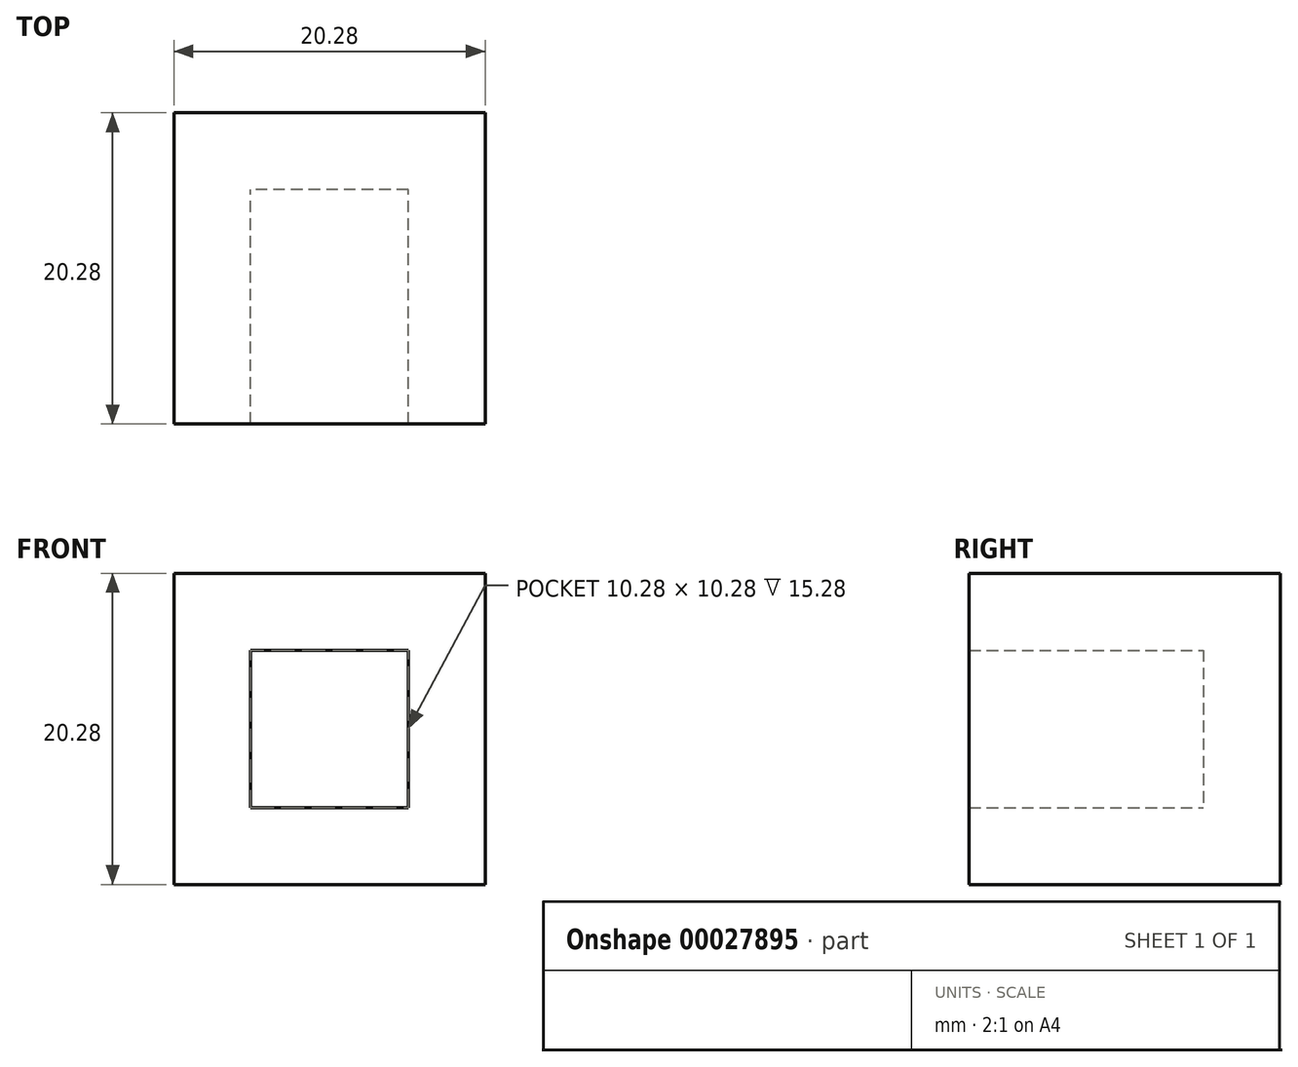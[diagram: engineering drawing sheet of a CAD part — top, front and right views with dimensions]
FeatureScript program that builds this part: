
annotation { "Feature Type Name" : "Feature", "Feature Type Description" : "" }
export const myFeature = defineFeature(function(context is Context, id is Id, definition is map)
    precondition{}
    {
        {
            var Q0;
            Q0=qCreatedBy(makeId("Front.planeOp"),FACE);
            var sketch = newSketch(context, id + "F0", { "sketchPlane" : qUnion([Q0])});
            skLineSegment(sketch, "E0.rect.bottom", {"start": v(10.14, 10.14) * mm, "end": v(-10.14, 10.14) * mm});
            skLineSegment(sketch, "E0.rect.top", {"start": v(10.14, -10.14) * mm, "end": v(-10.14, -10.14) * mm});
            skLineSegment(sketch, "E0.rect.left", {"start": v(10.14, 10.14) * mm, "end": v(10.14, -10.14) * mm});
            skLineSegment(sketch, "E0.rect.right", {"start": v(-10.14, 10.14) * mm, "end": v(-10.14, -10.14) * mm});
            skPoint(sketch, "E0.rect.middle", {"position": v(0, 0) * mm});
            skSolve(sketch);
        }
        {
            var Q0;
            Q0 = qSketchRegion(id + "F0", true);
            extrude(context, id + "F1", {"entities" : qUnion([Q0]), "depth" : 20.28 * mm});
        }
        {
            var Q0;
            Q0=makeQuery(id+"F1.opExtrude","CAP_FACE",FACE,{"disambiguationData":[OSD([sQuery(id+"F0.wireOp",EDGE,"E0.rect.bottom"),sQuery(id+"F0.wireOp",EDGE,"E0.rect.top"),sQuery(id+"F0.wireOp",EDGE,"E0.rect.left"),sQuery(id+"F0.wireOp",EDGE,"E0.rect.right")])],"isStart":false});
            shell(context, id + "F2", {"entities" : qUnion([Q0]), "thickness" : 5 * mm});
        }
    });
